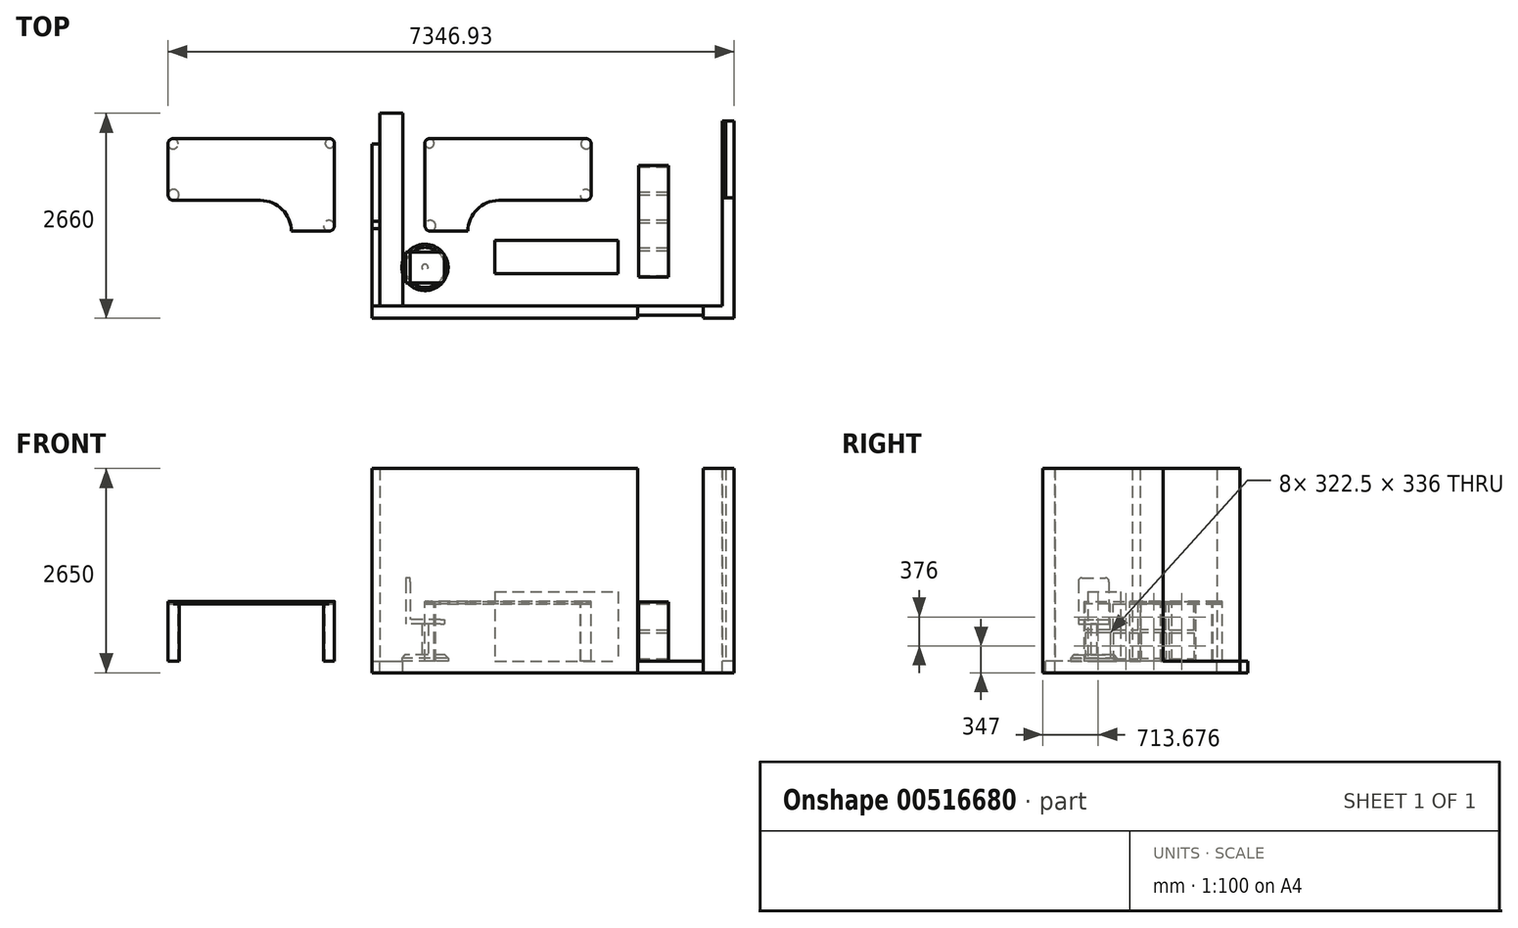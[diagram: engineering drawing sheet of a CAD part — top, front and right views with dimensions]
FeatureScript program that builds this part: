
annotation { "Feature Type Name" : "Feature", "Feature Type Description" : "" }
export const myFeature = defineFeature(function(context is Context, id is Id, definition is map)
    precondition{}
    {
        {
            var Q0;
            Q0=qCreatedBy(makeId("Top.planeOp"),FACE);
            var sketch = newSketch(context, id + "F0", { "sketchPlane" : qUnion([Q0])});
            skLineSegment(sketch, "E0.bottom", {"start": v(0, 0) * mm, "end": v(4450, 0) * mm});
            skLineSegment(sketch, "E0.top", {"start": v(0, 2500) * mm, "end": v(4450, 2500) * mm});
            skLineSegment(sketch, "E0.left", {"start": v(0, 0) * mm, "end": v(0, 2500) * mm});
            skLineSegment(sketch, "E0.right", {"start": v(4450, 0) * mm, "end": v(4450, 1400) * mm});
            skLineSegment(sketch, "E1", {"start": v(-100, 2660) * mm, "end": v(4600, 2660) * mm});
            skLineSegment(sketch, "E2", {"start": v(4600, 2660) * mm, "end": v(4600, 2400) * mm});
            skLineSegment(sketch, "E3", {"start": v(4600, 2400) * mm, "end": v(4450, 2400) * mm});
            skLineSegment(sketch, "E4", {"start": v(4450, 2400) * mm, "end": v(4450, 2500) * mm});
            skLineSegment(sketch, "E5", {"start": v(-100, -160) * mm, "end": v(4600, -160) * mm});
            skLineSegment(sketch, "E6", {"start": v(4600, -160) * mm, "end": v(4600, 1400) * mm});
            skLineSegment(sketch, "E7", {"start": v(4600, 1400) * mm, "end": v(4450, 1400) * mm});
            skLineSegment(sketch, "E8", {"start": v(-100, 2660) * mm, "end": v(-100, -160) * mm});
            skLineSegment(sketch, "E9", {"start": v(-100, 2100) * mm, "end": v(0, 2100) * mm});
            skLineSegment(sketch, "E10", {"start": v(-100, 1100) * mm, "end": v(0, 1100) * mm});
            skLineSegment(sketch, "E11", {"start": v(-100, 1000) * mm, "end": v(0, 1000) * mm});
            skLineSegment(sketch, "E12", {"start": v(300, 2500) * mm, "end": v(300, 0) * mm});
            skLineSegment(sketch, "E13", {"start": v(0, 0) * mm, "end": v(-100, 0) * mm});
            skLineSegment(sketch, "E14", {"start": v(4200, 0) * mm, "end": v(4200, -160) * mm});
            skLineSegment(sketch, "E15", {"start": v(3350, 0) * mm, "end": v(3350, -160) * mm});
            skLineSegment(sketch, "E16", {"start": v(4600, 2400) * mm, "end": v(4600, 1400) * mm});
            skLineSegment(sketch, "E17", {"start": v(4450, 2400) * mm, "end": v(4450, 1400) * mm});
            skLineSegment(sketch, "E18", {"start": v(4490, 2400) * mm, "end": v(4490, 1400) * mm});
            skLineSegment(sketch, "E19", {"start": v(3350, -160) * mm, "end": v(4200, -160) * mm});
            skLineSegment(sketch, "E20", {"start": v(3350, -120) * mm, "end": v(4200, -120) * mm});
            skSolve(sketch);
        }
        {
            var Q0;
            {var subQ3=sQuery(id+"F0.wireOp",EDGE,"E0.right");Q0=makeQuery(id+"F0.imprint","IMPRINT",FACE,{"disambiguationData":[TD([[makeQuery(id+"F0.imprint","IMPRINT",EDGE,{"derivedFrom":subQ3}),1.0]])]});}
            var Q1;
            {var subQ0=sQuery(id+"F0.wireOp",EDGE,"E1");Q1=makeQuery(id+"F0.imprint","IMPRINT",FACE,{"disambiguationData":[TD([[makeQuery(id+"F0.imprint","IMPRINT",EDGE,{"derivedFrom":subQ0}),-1.0]])]});}
            var Q2;
            {var subQ0=sQuery(id+"F0.wireOp",EDGE,"E9");Q2=makeQuery(id+"F0.imprint","IMPRINT",FACE,{"disambiguationData":[TD([[makeQuery(id+"F0.imprint","IMPRINT",EDGE,{"derivedFrom":subQ0}),-1.0]])]});}
            var Q3;
            {var subQ0=sQuery(id+"F0.wireOp",EDGE,"E10");Q3=makeQuery(id+"F0.imprint","IMPRINT",FACE,{"disambiguationData":[TD([[makeQuery(id+"F0.imprint","IMPRINT",EDGE,{"derivedFrom":subQ0}),-1.0]])]});}
            var Q4;
            {var subQ2=sQuery(id+"F0.wireOp",EDGE,"E11");Q4=makeQuery(id+"F0.imprint","IMPRINT",FACE,{"disambiguationData":[TD([[makeQuery(id+"F0.imprint","IMPRINT",EDGE,{"derivedFrom":subQ2}),-1.0]])]});}
            var Q5;
            {var subQ3=sQuery(id+"F0.wireOp",EDGE,"E13");Q5=makeQuery(id+"F0.imprint","IMPRINT",FACE,{"disambiguationData":[TD([[makeQuery(id+"F0.imprint","IMPRINT",EDGE,{"derivedFrom":subQ3}),1.0]])]});}
            var Q6;
            {var subQ0=sQuery(id+"F0.wireOp",EDGE,"E14");var subQ1=sQuery(id+"F0.wireOp",EDGE,"E0.bottom");var subQ2=makeQuery(id+"F0.imprint","INTERSECT",VERTEX,{"derivedFrom":[subQ1,subQ0]});Q6=makeQuery(id+"F0.imprint","IMPRINT",FACE,{"disambiguationData":[TD([[makeQuery(id+"F0.imprint","IMPRINT",EDGE,{"disambiguationData":[TD([[subQ2,1.0]])],"derivedFrom":subQ1}),-1.0]])]});}
            var Q7;
            {var subQ0=sQuery(id+"F0.wireOp",EDGE,"E19");Q7=makeQuery(id+"F0.imprint","IMPRINT",FACE,{"disambiguationData":[TD([[makeQuery(id+"F0.imprint","IMPRINT",EDGE,{"derivedFrom":subQ0}),1.0]])]});}
            var Q8;
            {var subQ4=sQuery(id+"F0.wireOp",EDGE,"E0.right");Q8=makeQuery(id+"F0.imprint","IMPRINT",FACE,{"disambiguationData":[TD([[makeQuery(id+"F0.imprint","IMPRINT",EDGE,{"derivedFrom":subQ4}),-1.0]])]});}
            var Q9;
            {var subQ0=sQuery(id+"F0.wireOp",EDGE,"E16");Q9=makeQuery(id+"F0.imprint","IMPRINT",FACE,{"disambiguationData":[TD([[makeQuery(id+"F0.imprint","IMPRINT",EDGE,{"derivedFrom":subQ0}),-1.0]])]});}
            var Q10;
            {var subQ0=sQuery(id+"F0.wireOp",EDGE,"E17");Q10=makeQuery(id+"F0.imprint","IMPRINT",FACE,{"disambiguationData":[TD([[makeQuery(id+"F0.imprint","IMPRINT",EDGE,{"derivedFrom":subQ0}),1.0]])]});}
            extrude(context, id + "F1", {"entities" : qUnion([Q0, Q1, Q2, Q3, Q4, Q5, Q6, Q7, Q8, Q9, Q10]), "oppositeDirection" : true, "depth" : 150 * mm, "offsetDistance" : 25 * mm});
        }
        {
            var Q0;
            {var subQ6=sQuery(id+"F0.wireOp",EDGE,"E12");Q0=makeQuery(id+"F0.imprint","IMPRINT",FACE,{"disambiguationData":[TD([[makeQuery(id+"F0.imprint","IMPRINT",EDGE,{"derivedFrom":subQ6}),-1.0]])]});}
            var Q1;
            Q1=makeQuery(id+"F1.opExtrude","CAP_FACE",FACE,{"disambiguationData":[OSD([sQuery(id+"F0.wireOp",EDGE,"E0.bottom"),sQuery(id+"F0.wireOp",EDGE,"E0.top"),sQuery(id+"F0.wireOp",EDGE,"E0.left"),sQuery(id+"F0.wireOp",EDGE,"E1"),sQuery(id+"F0.wireOp",EDGE,"E2"),sQuery(id+"F0.wireOp",EDGE,"E5"),sQuery(id+"F0.wireOp",EDGE,"E6"),sQuery(id+"F0.wireOp",EDGE,"E8"),sQuery(id+"F0.wireOp",EDGE,"E12"),sQuery(id+"F0.wireOp",EDGE,"E16"),sQuery(id+"F0.wireOp",EDGE,"E19")])],"isStart":false});
            extrude(context, id + "F2", {"entities" : qUnion([Q0]), "endBound" : BoundingType.UP_TO_SURFACE, "oppositeDirection" : true, "depth" : 25 * mm, "endBoundEntityFace" : qUnion([Q1]), "offsetDistance" : 25 * mm});
        }
        {
            var Q0;
            {var subQ0=sQuery(id+"F0.wireOp",EDGE,"E1");Q0=makeQuery(id+"F0.imprint","IMPRINT",FACE,{"disambiguationData":[TD([[makeQuery(id+"F0.imprint","IMPRINT",EDGE,{"derivedFrom":subQ0}),-1.0]])]});}
            var Q1;
            {var subQ4=sQuery(id+"F0.wireOp",EDGE,"E0.right");Q1=makeQuery(id+"F0.imprint","IMPRINT",FACE,{"disambiguationData":[TD([[makeQuery(id+"F0.imprint","IMPRINT",EDGE,{"derivedFrom":subQ4}),-1.0]])]});}
            var Q2;
            {var subQ3=sQuery(id+"F0.wireOp",EDGE,"E13");Q2=makeQuery(id+"F0.imprint","IMPRINT",FACE,{"disambiguationData":[TD([[makeQuery(id+"F0.imprint","IMPRINT",EDGE,{"derivedFrom":subQ3}),1.0]])]});}
            var Q3;
            {var subQ0=sQuery(id+"F0.wireOp",EDGE,"E10");Q3=makeQuery(id+"F0.imprint","IMPRINT",FACE,{"disambiguationData":[TD([[makeQuery(id+"F0.imprint","IMPRINT",EDGE,{"derivedFrom":subQ0}),-1.0]])]});}
            extrude(context, id + "F3", {"entities" : qUnion([Q0, Q1, Q2, Q3]), "operationType" : NewBodyOperationType.ADD, "depth" : 2500 * mm, "offsetDistance" : 25 * mm});
        }
        {
            var Q0;
            {var subQ0=sQuery(id+"F0.wireOp",EDGE,"E9");Q0=makeQuery(id+"F0.imprint","IMPRINT",FACE,{"disambiguationData":[TD([[makeQuery(id+"F0.imprint","IMPRINT",EDGE,{"derivedFrom":subQ0}),-1.0]])]});}
            var Q1;
            {var subQ2=sQuery(id+"F0.wireOp",EDGE,"E11");Q1=makeQuery(id+"F0.imprint","IMPRINT",FACE,{"disambiguationData":[TD([[makeQuery(id+"F0.imprint","IMPRINT",EDGE,{"derivedFrom":subQ2}),-1.0]])]});}
            var Q2;
            Q2=makeQuery(id+"F3.opExtrude","CAP_FACE",FACE,{"disambiguationData":[OSD([sQuery(id+"F0.wireOp",EDGE,"E0.top"),sQuery(id+"F0.wireOp",EDGE,"E0.left"),sQuery(id+"F0.wireOp",EDGE,"E1"),sQuery(id+"F0.wireOp",EDGE,"E2"),sQuery(id+"F0.wireOp",EDGE,"E3"),sQuery(id+"F0.wireOp",EDGE,"qMGoxhOv-Sapl-VxZx-tnCu-Dw4Tb1b8u0Ji"),sQuery(id+"F0.wireOp",EDGE,"E8"),sQuery(id+"F0.wireOp",EDGE,"E9"),sQuery(id+"F0.wireOp",EDGE,"E4")])],"isStart":false});
            extrude(context, id + "F4", {"entities" : qUnion([Q0, Q1]), "endBound" : BoundingType.UP_TO_SURFACE, "depth" : 25 * mm, "endBoundEntityFace" : qUnion([Q2]), "offsetDistance" : 25 * mm});
        }
        {
            var Q0;
            {var subQ0=sQuery(id+"F0.wireOp",EDGE,"E17");Q0=makeQuery(id+"F0.imprint","IMPRINT",FACE,{"disambiguationData":[TD([[makeQuery(id+"F0.imprint","IMPRINT",EDGE,{"derivedFrom":subQ0}),1.0]])]});}
            var Q1;
            {var subQ0=sQuery(id+"F0.wireOp",EDGE,"E19");Q1=makeQuery(id+"F0.imprint","IMPRINT",FACE,{"disambiguationData":[TD([[makeQuery(id+"F0.imprint","IMPRINT",EDGE,{"derivedFrom":subQ0}),1.0]])]});}
            var Q2;
            Q2=makeQuery(id+"F3.opExtrude","CAP_FACE",FACE,{"disambiguationData":[OSD([sQuery(id+"F0.wireOp",EDGE,"E0.top"),sQuery(id+"F0.wireOp",EDGE,"E0.left"),sQuery(id+"F0.wireOp",EDGE,"E1"),sQuery(id+"F0.wireOp",EDGE,"E2"),sQuery(id+"F0.wireOp",EDGE,"E3"),sQuery(id+"F0.wireOp",EDGE,"E8"),sQuery(id+"F0.wireOp",EDGE,"E9"),sQuery(id+"F0.wireOp",EDGE,"E4")])],"isStart":false});
            extrude(context, id + "F5", {"entities" : qUnion([Q0, Q1]), "endBound" : BoundingType.UP_TO_SURFACE, "depth" : 25 * mm, "endBoundEntityFace" : qUnion([Q2]), "offsetDistance" : 25 * mm});
        }
        {
            var Q0;
            Q0=qCreatedBy(makeId("Top.planeOp"),FACE);
            cPlane(context, id + "F6", {"entities" : qUnion([Q0]), "cplaneType" : CPlaneType.OFFSET, "offset" : 760 * mm, "width" : 150 * mm, "height" : 150 * mm});
        }
        {
            var Q0;
            Q0=qCreatedBy(id+"F6.planeOp",FACE);
            var sketch = newSketch(context, id + "F7", { "sketchPlane" : qUnion([Q0])});
            skLineSegment(sketch, "E21", {"start": v(646.45, 2169.46) * mm, "end": v(2680.38, 2169.46) * mm});
            skLineSegment(sketch, "E22", {"start": v(2746.93, 2102.92) * mm, "end": v(2746.93, 1441.14) * mm});
            skLineSegment(sketch, "E23", {"start": v(2675.25, 1369.46) * mm, "end": v(1546.93, 1369.46) * mm});
            skLineSegment(sketch, "E24", {"start": v(1146.93, 969.46) * mm, "end": v(1146.93, 969.46) * mm});
            skLineSegment(sketch, "E25", {"start": v(1146.93, 969.46) * mm, "end": v(657.67, 969.46) * mm});
            skLineSegment(sketch, "E26", {"start": v(586.93, 1040.2) * mm, "end": v(586.93, 2109.94) * mm});
            skPoint(sketch, "E27.visualSharp", {"position": v(1146.93, 1369.46) * mm});
            skArc(sketch, "E27.filletArc", {"start": v(1546.93, 1369.46) * mm, "mid": v(1264.08, 1252.3) * mm, "end": v(1146.93, 969.46) * mm});
            skCircle(sketch, "E28", {"center": v(646.45, 2109.94) * mm, "radius": 59.52 * mm});
            skCircle(sketch, "E29", {"center": v(657.67, 1040.2) * mm, "radius": 70.74 * mm});
            skCircle(sketch, "E30", {"center": v(2680.38, 2102.92) * mm, "radius": 66.55 * mm});
            skCircle(sketch, "E31", {"center": v(2675.25, 1441.14) * mm, "radius": 71.67 * mm});
            skPoint(sketch, "E32.orphan", {"position": v(586.93, 969.46) * mm});
            skPoint(sketch, "E33.orphan", {"position": v(586.93, 2169.46) * mm});
            skSolve(sketch);
        }
        {
            var Q0;
            Q0=makeQuery(id+"F7.imprint","IMPRINT",FACE,{"disambiguationData":[TD([[makeQuery(id+"F7.imprint","IMPRINT",EDGE,{"derivedFrom":sQuery(id+"F7.wireOp",EDGE,"E21")}),-1.0]])]});
            var Q1;
            Q1=makeQuery(id+"F7.imprint","IMPRINT",FACE,{"disambiguationData":[TD([[makeQuery(id+"F7.imprint","IMPRINT",EDGE,{"derivedFrom":sQuery(id+"F7.wireOp",EDGE,"E28")}),1.0]])]});
            var Q2;
            Q2=makeQuery(id+"F7.imprint","IMPRINT",FACE,{"disambiguationData":[TD([[makeQuery(id+"F7.imprint","IMPRINT",EDGE,{"derivedFrom":sQuery(id+"F7.wireOp",EDGE,"E30")}),1.0]])]});
            var Q3;
            Q3=makeQuery(id+"F7.imprint","IMPRINT",FACE,{"disambiguationData":[TD([[makeQuery(id+"F7.imprint","IMPRINT",EDGE,{"derivedFrom":sQuery(id+"F7.wireOp",EDGE,"E31")}),1.0]])]});
            var Q4;
            Q4=makeQuery(id+"F7.imprint","IMPRINT",FACE,{"disambiguationData":[TD([[makeQuery(id+"F7.imprint","IMPRINT",EDGE,{"derivedFrom":sQuery(id+"F7.wireOp",EDGE,"E29")}),1.0]])]});
            extrude(context, id + "F8", {"entities" : qUnion([Q0, Q1, Q2, Q3, Q4]), "oppositeDirection" : true, "depth" : 30 * mm, "offsetDistance" : 25 * mm, "symmetric" : true});
        }
        {
            var Q0;
            Q0=makeQuery(id+"F7.imprint","IMPRINT",FACE,{"disambiguationData":[TD([[makeQuery(id+"F7.imprint","IMPRINT",EDGE,{"derivedFrom":sQuery(id+"F7.wireOp",EDGE,"E28")}),1.0]])]});
            var Q1;
            Q1=makeQuery(id+"F7.imprint","IMPRINT",FACE,{"disambiguationData":[TD([[makeQuery(id+"F7.imprint","IMPRINT",EDGE,{"derivedFrom":sQuery(id+"F7.wireOp",EDGE,"E30")}),1.0]])]});
            var Q2;
            Q2=makeQuery(id+"F7.imprint","IMPRINT",FACE,{"disambiguationData":[TD([[makeQuery(id+"F7.imprint","IMPRINT",EDGE,{"derivedFrom":sQuery(id+"F7.wireOp",EDGE,"E31")}),1.0]])]});
            var Q3;
            Q3=makeQuery(id+"F7.imprint","IMPRINT",FACE,{"disambiguationData":[TD([[makeQuery(id+"F7.imprint","IMPRINT",EDGE,{"derivedFrom":sQuery(id+"F7.wireOp",EDGE,"E29")}),1.0]])]});
            var Q4;
            Q4=sQuery(id+"F7.wireOp",EDGE,"E29");
            var Q5;
            Q5=sQuery(id+"F7.wireOp",EDGE,"E28");
            var Q6;
            Q6=sQuery(id+"F7.wireOp",EDGE,"E30");
            var Q7;
            Q7=sQuery(id+"F7.wireOp",EDGE,"E31");
            var Q8;
            {var subQ0=sQuery(id+"F0.wireOp",EDGE,"E12");var subQ1=sQuery(id+"F0.wireOp",EDGE,"E0.left");var subQ2=sQuery(id+"F0.wireOp",EDGE,"E0.top");var subQ3=sQuery(id+"F0.wireOp",EDGE,"E0.bottom");Q8=makeQuery(id+"F3.boolean.opBoolean","MERGE",FACE,{"derivedFrom":[makeQuery(id+"F1.opExtrude","CAP_FACE",FACE,{"disambiguationData":[OSD([subQ3,subQ2,subQ1,sQuery(id+"F0.wireOp",EDGE,"E1"),sQuery(id+"F0.wireOp",EDGE,"E2"),sQuery(id+"F0.wireOp",EDGE,"E5"),sQuery(id+"F0.wireOp",EDGE,"E6"),sQuery(id+"F0.wireOp",EDGE,"E8"),subQ0,sQuery(id+"F0.wireOp",EDGE,"E16"),sQuery(id+"F0.wireOp",EDGE,"E19")])],"isStart":true}),makeQuery(id+"F2.opExtrude","CAP_FACE",FACE,{"disambiguationData":[OSD([subQ3,subQ2,subQ1,subQ0])],"isStart":true})]});}
            extrude(context, id + "F9", {"entities" : qUnion([Q0, Q1, Q2, Q3]), "operationType" : NewBodyOperationType.ADD, "surfaceEntities" : qUnion([Q4, Q5, Q6, Q7]), "endBound" : BoundingType.UP_TO_SURFACE, "oppositeDirection" : true, "depth" : 25 * mm, "endBoundEntityFace" : qUnion([Q8]), "offsetDistance" : 25 * mm});
        }
        {
            var Q0;
            Q0=makeQuery(id+"F8.opExtrude","SWEPT_BODY",BODY,{"disambiguationData":[OSD([sQuery(id+"F7.wireOp",EDGE,"E21"),sQuery(id+"F7.wireOp",EDGE,"E22"),sQuery(id+"F7.wireOp",EDGE,"E23"),sQuery(id+"F7.wireOp",EDGE,"E25"),sQuery(id+"F7.wireOp",EDGE,"E26"),sQuery(id+"F7.wireOp",EDGE,"E27.filletArc")])]});
            var Q1;
            Q1=qCreatedBy(makeId("Right.planeOp"),FACE);
            mirror(context, id + "F10", {"entities" : qUnion([Q0]), "mirrorPlane" : qUnion([Q1])});
        }
        {
            var Q0;
            Q0=qCreatedBy(makeId("Top.planeOp"),FACE);
            var sketch = newSketch(context, id + "F11", { "sketchPlane" : qUnion([Q0])});
            skLineSegment(sketch, "E34.bottom", {"start": v(1496.36, 419.88) * mm, "end": v(3096.36, 419.88) * mm});
            skLineSegment(sketch, "E34.top", {"start": v(1496.36, 849.88) * mm, "end": v(3096.36, 849.88) * mm});
            skLineSegment(sketch, "E34.left", {"start": v(1496.36, 419.88) * mm, "end": v(1496.36, 849.88) * mm});
            skLineSegment(sketch, "E34.right", {"start": v(3096.36, 419.88) * mm, "end": v(3096.36, 849.88) * mm});
            skSolve(sketch);
        }
        {
            var Q0;
            Q0 = qSketchRegion(id + "F11", true);
            extrude(context, id + "F12", {"entities" : qUnion([Q0]), "depth" : 900 * mm, "offsetDistance" : 25 * mm});
        }
        {
            var Q0;
            Q0=qCreatedBy(makeId("Top.planeOp"),FACE);
            var sketch = newSketch(context, id + "F13", { "sketchPlane" : qUnion([Q0])});
            skLineSegment(sketch, "E35.bottom", {"start": v(3360.97, 1822.43) * mm, "end": v(3750.97, 1822.43) * mm});
            skLineSegment(sketch, "E35.top", {"start": v(3360.97, 372.43) * mm, "end": v(3750.97, 372.43) * mm});
            skLineSegment(sketch, "E35.left", {"start": v(3360.97, 1822.43) * mm, "end": v(3360.97, 372.43) * mm});
            skLineSegment(sketch, "E35.right", {"start": v(3750.97, 1822.43) * mm, "end": v(3750.97, 372.43) * mm});
            skSolve(sketch);
        }
        {
            var Q0;
            Q0 = qSketchRegion(id + "F13", true);
            extrude(context, id + "F14", {"entities" : qUnion([Q0]), "depth" : 770 * mm, "offsetDistance" : 25 * mm});
        }
        {
            var Q0;
            Q0=makeQuery(id+"F14.opExtrude","SWEPT_FACE",FACE,{"disambiguationData":[OSD([sQuery(id+"F13.wireOp",EDGE,"E35.right")])]});
            var sketch = newSketch(context, id + "F15", { "sketchPlane" : qUnion([Q0])});
            skLineSegment(sketch, "E36", {"start": v(372.43, 385) * mm, "end": v(1822.43, 385) * mm, "construction": true});
            skLineSegment(sketch, "E37", {"start": v(1097.43, 770) * mm, "end": v(1097.43, 0) * mm, "construction": true});
            skLineSegment(sketch, "E38", {"start": v(734.93, 770) * mm, "end": v(734.93, 0) * mm, "construction": true});
            skLineSegment(sketch, "E39", {"start": v(1459.93, 770) * mm, "end": v(1459.93, 0) * mm, "construction": true});
            skLineSegment(sketch, "E40.bottom", {"start": v(392.43, 741) * mm, "end": v(714.93, 741) * mm});
            skLineSegment(sketch, "E40.top", {"start": v(392.43, 405) * mm, "end": v(714.93, 405) * mm});
            skLineSegment(sketch, "E40.left", {"start": v(392.43, 741) * mm, "end": v(392.43, 405) * mm});
            skLineSegment(sketch, "E40.right", {"start": v(714.93, 741) * mm, "end": v(714.93, 405) * mm});
            skLineSegment(sketch, "E41.MirrorCS", {"start": v(754.93, 741) * mm, "end": v(754.93, 405) * mm});
            skLineSegment(sketch, "E42.MirrorCS", {"start": v(1077.43, 741) * mm, "end": v(754.93, 741) * mm});
            skLineSegment(sketch, "E43.MirrorCS", {"start": v(1077.43, 741) * mm, "end": v(1077.43, 405) * mm});
            skLineSegment(sketch, "E44.MirrorCS", {"start": v(1077.43, 405) * mm, "end": v(754.93, 405) * mm});
            skLineSegment(sketch, "E45.MirrorCS", {"start": v(1077.43, 365) * mm, "end": v(754.93, 365) * mm});
            skLineSegment(sketch, "E46.MirrorCS", {"start": v(1077.43, 29) * mm, "end": v(754.93, 29) * mm});
            skLineSegment(sketch, "E47.MirrorCS", {"start": v(754.93, 29) * mm, "end": v(754.93, 365) * mm});
            skLineSegment(sketch, "E48.MirrorCS", {"start": v(1077.43, 29) * mm, "end": v(1077.43, 365) * mm});
            skLineSegment(sketch, "E49.MirrorCS", {"start": v(714.93, 29) * mm, "end": v(714.93, 365) * mm});
            skLineSegment(sketch, "E50.MirrorCS", {"start": v(392.43, 29) * mm, "end": v(714.93, 29) * mm});
            skLineSegment(sketch, "E51.MirrorCS", {"start": v(392.43, 29) * mm, "end": v(392.43, 365) * mm});
            skLineSegment(sketch, "E52.MirrorCS", {"start": v(392.43, 365) * mm, "end": v(714.93, 365) * mm});
            skLineSegment(sketch, "E53.MirrorCS", {"start": v(1117.43, 741) * mm, "end": v(1117.43, 405) * mm});
            skLineSegment(sketch, "E54.MirrorCS", {"start": v(1439.93, 741) * mm, "end": v(1439.93, 405) * mm});
            skLineSegment(sketch, "E55.MirrorCS", {"start": v(1479.93, 741) * mm, "end": v(1479.93, 405) * mm});
            skLineSegment(sketch, "E56.MirrorCS", {"start": v(1802.43, 741) * mm, "end": v(1802.43, 405) * mm});
            skLineSegment(sketch, "E57.MirrorCS", {"start": v(1802.43, 741) * mm, "end": v(1479.93, 741) * mm});
            skLineSegment(sketch, "E58.MirrorCS", {"start": v(1117.43, 741) * mm, "end": v(1439.93, 741) * mm});
            skLineSegment(sketch, "E59.MirrorCS", {"start": v(1802.43, 405) * mm, "end": v(1479.93, 405) * mm});
            skLineSegment(sketch, "E60.MirrorCS", {"start": v(1117.43, 405) * mm, "end": v(1439.93, 405) * mm});
            skLineSegment(sketch, "E61.MirrorCS", {"start": v(1117.43, 29) * mm, "end": v(1117.43, 365) * mm});
            skLineSegment(sketch, "E62.MirrorCS", {"start": v(1439.93, 29) * mm, "end": v(1439.93, 365) * mm});
            skLineSegment(sketch, "E63.MirrorCS", {"start": v(1479.93, 29) * mm, "end": v(1479.93, 365) * mm});
            skLineSegment(sketch, "E64.MirrorCS", {"start": v(1802.43, 29) * mm, "end": v(1802.43, 365) * mm});
            skLineSegment(sketch, "E65.MirrorCS", {"start": v(1802.43, 365) * mm, "end": v(1479.93, 365) * mm});
            skLineSegment(sketch, "E66.MirrorCS", {"start": v(1117.43, 365) * mm, "end": v(1439.93, 365) * mm});
            skLineSegment(sketch, "E67.MirrorCS", {"start": v(1117.43, 29) * mm, "end": v(1439.93, 29) * mm});
            skLineSegment(sketch, "E68.MirrorCS", {"start": v(1802.43, 29) * mm, "end": v(1479.93, 29) * mm});
            skSolve(sketch);
        }
        {
            var Q0;
            Q0 = qSketchRegion(id + "F15", true);
            extrude(context, id + "F16", {"entities" : qUnion([Q0]), "operationType" : NewBodyOperationType.REMOVE, "endBound" : BoundingType.UP_TO_NEXT, "oppositeDirection" : true, "depth" : 25 * mm, "offsetDistance" : 25 * mm});
        }
        {
            var Q0;
            Q0=qCreatedBy(makeId("Top.planeOp"),FACE);
            var sketch = newSketch(context, id + "F17", { "sketchPlane" : qUnion([Q0])});
            skCircle(sketch, "E69", {"center": v(588.95, 499.4) * mm, "radius": 300 * mm});
            skSolve(sketch);
        }
        {
            var Q0;
            Q0 = qSketchRegion(id + "F17", true);
            extrude(context, id + "F18", {"entities" : qUnion([Q0]), "depth" : 80 * mm, "offsetDistance" : 25 * mm});
        }
        {
            var Q0;
            Q0=makeQuery(id+"F18.opExtrude","CAP_FACE",FACE,{"disambiguationData":[OSD([sQuery(id+"F17.wireOp",EDGE,"E69")])],"isStart":false});
            var sketch = newSketch(context, id + "F19", { "sketchPlane" : qUnion([Q0])});
            skCircle(sketch, "E70", {"center": v(588.95, 499.4) * mm, "radius": 40 * mm});
            skSolve(sketch);
        }
        {
            var Q0;
            Q0 = qSketchRegion(id + "F19", true);
            extrude(context, id + "F20", {"entities" : qUnion([Q0]), "operationType" : NewBodyOperationType.ADD, "depth" : 400 * mm, "offsetDistance" : 25 * mm});
        }
        {
            var Q0;
            Q0=makeQuery(id+"F20.opExtrude","CAP_FACE",FACE,{"disambiguationData":[OSD([sQuery(id+"F19.wireOp",EDGE,"E70")])],"isStart":false});
            var sketch = newSketch(context, id + "F21", { "sketchPlane" : qUnion([Q0])});
            skLineSegment(sketch, "E71.bottom", {"start": v(838.95, 299.4) * mm, "end": v(338.95, 299.4) * mm});
            skLineSegment(sketch, "E71.top", {"start": v(838.95, 699.4) * mm, "end": v(338.95, 699.4) * mm});
            skLineSegment(sketch, "E71.left", {"start": v(838.95, 299.4) * mm, "end": v(838.95, 699.4) * mm});
            skLineSegment(sketch, "E71.right", {"start": v(338.95, 299.4) * mm, "end": v(338.95, 699.4) * mm});
            skPoint(sketch, "E71.middle", {"position": v(588.95, 499.4) * mm});
            skLineSegment(sketch, "E72", {"start": v(398.95, 699.4) * mm, "end": v(398.95, 299.4) * mm});
            skSolve(sketch);
        }
        {
            var Q0;
            Q0 = qSketchRegion(id + "F21", true);
            extrude(context, id + "F22", {"entities" : qUnion([Q0]), "operationType" : NewBodyOperationType.ADD, "depth" : 60 * mm, "offsetDistance" : 25 * mm});
        }
        {
            var Q0;
            {var subQ0=sQuery(id+"F21.wireOp",EDGE,"E71.right");Q0=makeQuery(id+"F21.imprint","IMPRINT",FACE,{"disambiguationData":[TD([[makeQuery(id+"F21.imprint","IMPRINT",EDGE,{"derivedFrom":subQ0}),-1.0]])]});}
            extrude(context, id + "F23", {"entities" : qUnion([Q0]), "operationType" : NewBodyOperationType.ADD, "depth" : 600 * mm, "offsetDistance" : 25 * mm});
        }
        {
            var Q0;
            Q0=makeQuery(id+"F22.opExtrude","SWEPT_EDGE",EDGE,{"disambiguationData":[OSD([sQuery(id+"F21.wireOp",EDGE,"E71.top"),sQuery(id+"F21.wireOp",EDGE,"E71.left")])]});
            var Q1;
            Q1=makeQuery(id+"F22.opExtrude","SWEPT_EDGE",EDGE,{"disambiguationData":[OSD([sQuery(id+"F21.wireOp",EDGE,"E71.bottom"),sQuery(id+"F21.wireOp",EDGE,"E71.left")])]});
            var Q2;
            Q2=makeQuery(id+"F23.opExtrude","CAP_EDGE",EDGE,{"disambiguationData":[OSD([sQuery(id+"F21.wireOp",EDGE,"E71.bottom")])],"isStart":false});
            var Q3;
            Q3=makeQuery(id+"F23.opExtrude","CAP_EDGE",EDGE,{"disambiguationData":[OSD([sQuery(id+"F21.wireOp",EDGE,"E71.top")])],"isStart":false});
            fillet(context, id + "F24", {"entities" : qUnion([Q0, Q1, Q2, Q3]), "radius" : 50 * mm, "tangentPropagation" : true, "allowEdgeOverflow" : false});
        }
        {
            var Q0;
            Q0=makeQuery(id+"F18.opExtrude","CAP_EDGE",EDGE,{"disambiguationData":[OSD([sQuery(id+"F17.wireOp",EDGE,"E69")])],"isStart":false});
            chamfer(context, id + "F25", {"entities" : qUnion([Q0]), "width" : 40 * mm, "tangentPropagation" : true});
        }
    });
